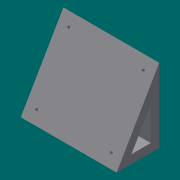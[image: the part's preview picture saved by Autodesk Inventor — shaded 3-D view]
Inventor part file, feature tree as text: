
AUTODESK INVENTOR PART (.ipt)
format: ipt  version: 2013 (Build 170138000, 138)  size: 132,608 bytes
history: native  units: mm
features: sketch x5, extrude x3, hole x2, other x1
ambient origin geometry x8: Origin, YZ Plane, XZ Plane, XY Plane, X Axis, Y Axis, Z Axis, Center Point
feature tree (11):
  other  "ソリッド1"
  extrude  "押し出し1"  Depth=80.0mm
  hole  "穴1"  [1 undecoded]
  hole  "穴2"  [1 undecoded]
  extrude  "押し出し2"  Depth=90.0mm TaperAngle=0.0deg
  extrude  "押し出し3"  Depth=10.0mm
  sketch  "スケッチ1"
  sketch  "スケッチ2"
  sketch  "スケッチ3"
  sketch  "スケッチ4"
  sketch  "スケッチ5"
note: 2 required parameter values undecoded (feature->parameter linkage not recoverable at this tier; creation-order binding heuristic only, values carry confidence <= 0.55)
